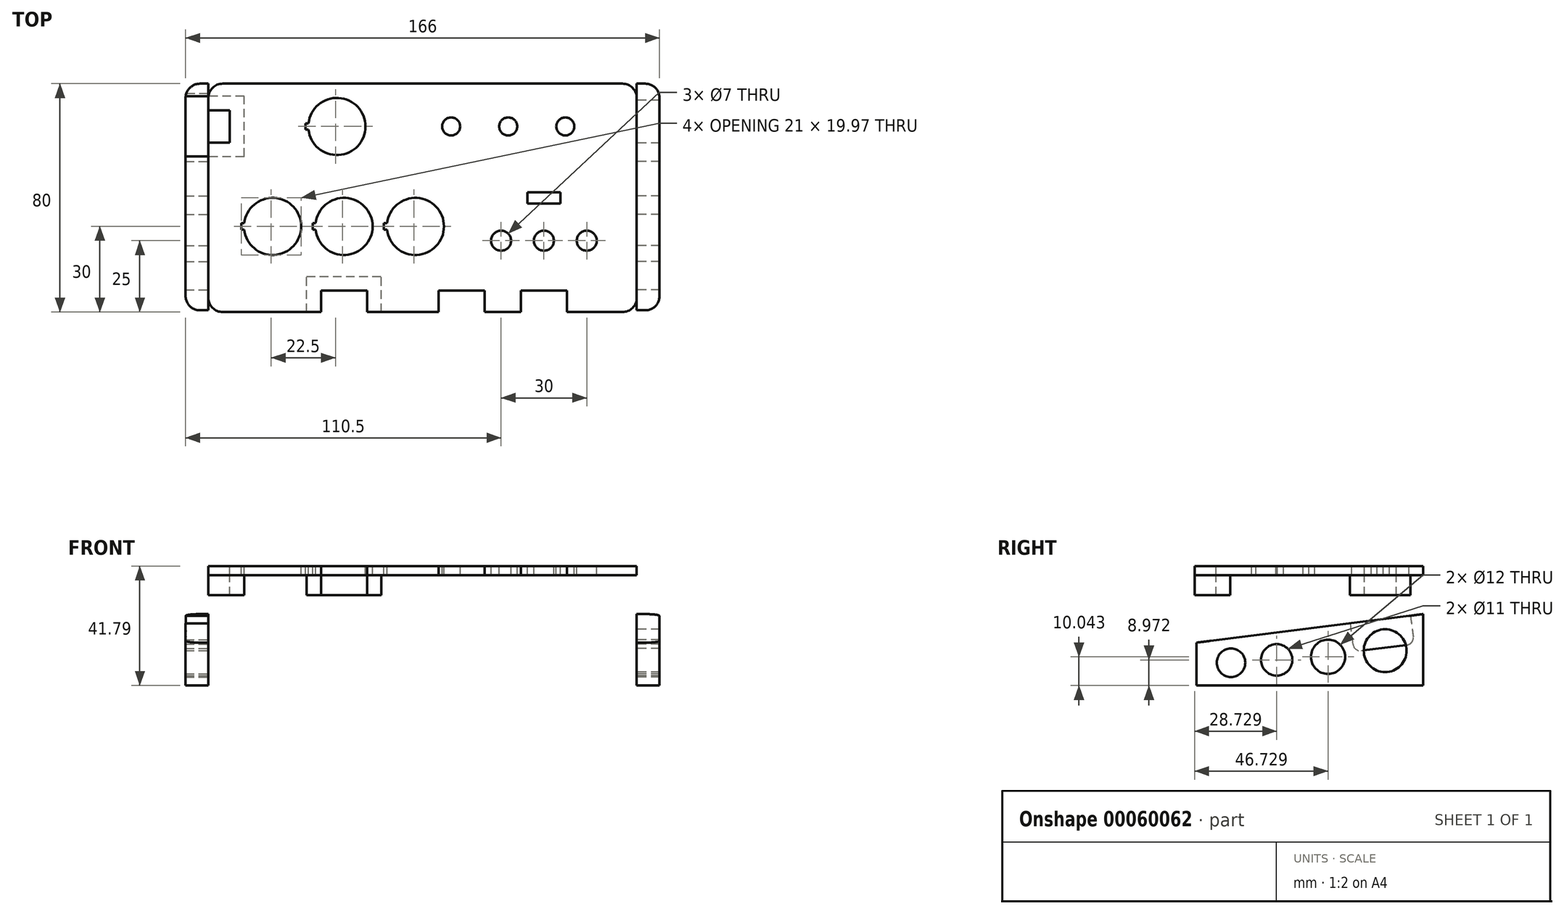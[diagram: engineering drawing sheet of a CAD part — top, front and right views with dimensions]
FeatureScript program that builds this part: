
annotation { "Feature Type Name" : "Feature", "Feature Type Description" : "" }
export const myFeature = defineFeature(function(context is Context, id is Id, definition is map)
    precondition{}
    {
        {
            var Q0;
            Q0=qCreatedBy(makeId("Top.planeOp"),FACE);
            var sketch = newSketch(context, id + "F0", { "sketchPlane" : qUnion([Q0])});
            skLineSegment(sketch, "E0.rect.bottom", {"start": v(75, 40) * mm, "end": v(-75, 40) * mm});
            skLineSegment(sketch, "E0.rect.top", {"start": v(75, -40) * mm, "end": v(-75, -40) * mm});
            skLineSegment(sketch, "E0.rect.left", {"start": v(75, 40) * mm, "end": v(75, -40) * mm});
            skLineSegment(sketch, "E0.rect.right", {"start": v(-75, 40) * mm, "end": v(-75, -40) * mm});
            skPoint(sketch, "E0.rect.middle", {"position": v(0, 0) * mm});
            skSolve(sketch);
        }
        {
            var Q0;
            Q0 = qSketchRegion(id + "F0", true);
            extrude(context, id + "F1", {"entities" : qUnion([Q0]), "depth" : 3.17 * mm});
        }
        {
            var Q0;
            Q0=makeQuery(id+"F1.opExtrude","SWEPT_EDGE",EDGE,{"disambiguationData":[OSD([sQuery(id+"F0.wireOp",EDGE,"E0.rect.bottom"),sQuery(id+"F0.wireOp",EDGE,"E0.rect.right")])]});
            var Q1;
            Q1=makeQuery(id+"F1.opExtrude","SWEPT_EDGE",EDGE,{"disambiguationData":[OSD([sQuery(id+"F0.wireOp",EDGE,"E0.rect.top"),sQuery(id+"F0.wireOp",EDGE,"E0.rect.right")])]});
            var Q2;
            Q2=makeQuery(id+"F1.opExtrude","SWEPT_EDGE",EDGE,{"disambiguationData":[OSD([sQuery(id+"F0.wireOp",EDGE,"E0.rect.top"),sQuery(id+"F0.wireOp",EDGE,"E0.rect.left")])]});
            var Q3;
            Q3=makeQuery(id+"F1.opExtrude","SWEPT_EDGE",EDGE,{"disambiguationData":[OSD([sQuery(id+"F0.wireOp",EDGE,"E0.rect.bottom"),sQuery(id+"F0.wireOp",EDGE,"E0.rect.left")])]});
            fillet(context, id + "F2", {"entities" : qUnion([Q0, Q1, Q2, Q3]), "radius" : 5 * mm, "tangentPropagation" : true, "allowEdgeOverflow" : false});
        }
        {
            var Q0;
            Q0=makeQuery(id+"F1.opExtrude","CAP_FACE",FACE,{"disambiguationData":[OSD([sQuery(id+"F0.wireOp",EDGE,"E0.rect.bottom"),sQuery(id+"F0.wireOp",EDGE,"E0.rect.top"),sQuery(id+"F0.wireOp",EDGE,"E0.rect.left"),sQuery(id+"F0.wireOp",EDGE,"E0.rect.right")])],"isStart":false});
            var sketch = newSketch(context, id + "F3", { "sketchPlane" : qUnion([Q0])});
            skArc(sketch, "E1", {"start": v(-39.94, 23.9) * mm, "mid": v(-20, 25) * mm, "end": v(-39.94, 26.1) * mm});
            skArc(sketch, "E2", {"start": v(-62.44, -11.1) * mm, "mid": v(-42.5, -10) * mm, "end": v(-62.44, -8.9) * mm});
            skArc(sketch, "E3", {"start": v(-37.44, -11.1) * mm, "mid": v(-17.5, -10) * mm, "end": v(-37.44, -8.9) * mm});
            skArc(sketch, "E4", {"start": v(-12.44, -11.1) * mm, "mid": v(7.5, -10) * mm, "end": v(-12.44, -8.9) * mm});
            skCircle(sketch, "E5", {"center": v(27.5, -15) * mm, "radius": 3.5 * mm});
            skCircle(sketch, "E6", {"center": v(42.5, -15) * mm, "radius": 3.5 * mm});
            skCircle(sketch, "E7", {"center": v(57.5, -15) * mm, "radius": 3.5 * mm});
            skCircle(sketch, "E8", {"center": v(10, 25) * mm, "radius": 3.18 * mm});
            skCircle(sketch, "E9", {"center": v(30, 25) * mm, "radius": 3.18 * mm});
            skCircle(sketch, "E10", {"center": v(50, 25) * mm, "radius": 3.18 * mm});
            skLineSegment(sketch, "E11", {"start": v(20, 17.63) * mm, "end": v(20, -10) * mm, "construction": true});
            skLineSegment(sketch, "E12.rect.bottom", {"start": v(48.3, 2) * mm, "end": v(36.7, 2) * mm});
            skLineSegment(sketch, "E12.rect.top", {"start": v(48.3, -2) * mm, "end": v(36.7, -2) * mm});
            skLineSegment(sketch, "E12.rect.left", {"start": v(48.3, 2) * mm, "end": v(48.3, -2) * mm});
            skLineSegment(sketch, "E12.rect.right", {"start": v(36.7, 2) * mm, "end": v(36.7, -2) * mm});
            skPoint(sketch, "E12.rect.middle", {"position": v(42.5, 0) * mm});
            skLineSegment(sketch, "E13.top", {"start": v(-63.5, -11.1) * mm, "end": v(-63.5, -8.9) * mm});
            skLineSegment(sketch, "E13.left", {"start": v(-62.44, -11.1) * mm, "end": v(-63.5, -11.1) * mm});
            skLineSegment(sketch, "E13.right", {"start": v(-62.44, -8.9) * mm, "end": v(-63.5, -8.9) * mm});
            skLineSegment(sketch, "E14.top", {"start": v(-38.5, -11.1) * mm, "end": v(-38.5, -8.9) * mm});
            skLineSegment(sketch, "E14.left", {"start": v(-37.44, -11.1) * mm, "end": v(-38.5, -11.1) * mm});
            skLineSegment(sketch, "E14.right", {"start": v(-37.44, -8.9) * mm, "end": v(-38.5, -8.9) * mm});
            skLineSegment(sketch, "E15.top", {"start": v(-13.5, -11.1) * mm, "end": v(-13.5, -8.9) * mm});
            skLineSegment(sketch, "E15.left", {"start": v(-12.44, -11.1) * mm, "end": v(-13.5, -11.1) * mm});
            skLineSegment(sketch, "E15.right", {"start": v(-12.44, -8.9) * mm, "end": v(-13.5, -8.9) * mm});
            skLineSegment(sketch, "E16.bottom", {"start": v(-39.94, 26.1) * mm, "end": v(-41, 26.1) * mm});
            skLineSegment(sketch, "E16.top", {"start": v(-39.94, 23.9) * mm, "end": v(-41, 23.9) * mm});
            skLineSegment(sketch, "E16.right", {"start": v(-41, 26.1) * mm, "end": v(-41, 23.9) * mm});
            skSolve(sketch);
        }
        {
            var Q0;
            Q0 = qSketchRegion(id + "F3", true);
            extrude(context, id + "F4", {"entities" : qUnion([Q0]), "operationType" : NewBodyOperationType.REMOVE, "endBound" : BoundingType.THROUGH_ALL, "oppositeDirection" : true, "depth" : 25 * mm});
        }
        {
            var Q0;
            Q0=makeQuery(id+"F1.opExtrude","CAP_FACE",FACE,{"disambiguationData":[OSD([sQuery(id+"F0.wireOp",EDGE,"E0.rect.bottom"),sQuery(id+"F0.wireOp",EDGE,"E0.rect.top"),sQuery(id+"F0.wireOp",EDGE,"E0.rect.left"),sQuery(id+"F0.wireOp",EDGE,"E0.rect.right")])],"isStart":false});
            var sketch = newSketch(context, id + "F5", { "sketchPlane" : qUnion([Q0])});
            skLineSegment(sketch, "E17.bottom", {"start": v(-75, 30.6) * mm, "end": v(-67.5, 30.6) * mm});
            skLineSegment(sketch, "E17.top", {"start": v(-75, 19.4) * mm, "end": v(-67.5, 19.4) * mm});
            skLineSegment(sketch, "E17.left", {"start": v(-75, 30.6) * mm, "end": v(-75, 19.4) * mm});
            skLineSegment(sketch, "E17.right", {"start": v(-67.5, 30.6) * mm, "end": v(-67.5, 19.4) * mm});
            skLineSegment(sketch, "E18", {"start": v(-67.5, 25) * mm, "end": v(-30, 25) * mm, "construction": true});
            skLineSegment(sketch, "E19.bottom", {"start": v(-35.6, -40) * mm, "end": v(-19.4, -40) * mm});
            skLineSegment(sketch, "E19.top", {"start": v(-35.6, -32.5) * mm, "end": v(-19.4, -32.5) * mm});
            skLineSegment(sketch, "E19.left", {"start": v(-35.6, -40) * mm, "end": v(-35.6, -32.5) * mm});
            skLineSegment(sketch, "E19.right", {"start": v(-19.4, -40) * mm, "end": v(-19.4, -32.5) * mm});
            skLineSegment(sketch, "E20.bottom", {"start": v(34.4, -40) * mm, "end": v(50.6, -40) * mm});
            skLineSegment(sketch, "E20.top", {"start": v(34.4, -32.5) * mm, "end": v(50.6, -32.5) * mm});
            skLineSegment(sketch, "E20.left", {"start": v(34.4, -40) * mm, "end": v(34.4, -32.5) * mm});
            skLineSegment(sketch, "E20.right", {"start": v(50.6, -40) * mm, "end": v(50.6, -32.5) * mm});
            skLineSegment(sketch, "E21.bottom", {"start": v(5.6, -40) * mm, "end": v(21.8, -40) * mm});
            skLineSegment(sketch, "E21.top", {"start": v(5.6, -32.5) * mm, "end": v(21.8, -32.5) * mm});
            skLineSegment(sketch, "E21.left", {"start": v(5.6, -40) * mm, "end": v(5.6, -32.5) * mm});
            skLineSegment(sketch, "E21.right", {"start": v(21.8, -40) * mm, "end": v(21.8, -32.5) * mm});
            skLineSegment(sketch, "E22", {"start": v(-27.5, -10) * mm, "end": v(-27.5, -32.5) * mm, "construction": true});
            skLineSegment(sketch, "E23", {"start": v(42.5, -15) * mm, "end": v(42.5, -32.5) * mm, "construction": true});
            skSolve(sketch);
        }
        {
            var Q0;
            Q0 = qSketchRegion(id + "F5", true);
            extrude(context, id + "F6", {"entities" : qUnion([Q0]), "operationType" : NewBodyOperationType.REMOVE, "endBound" : BoundingType.THROUGH_ALL, "oppositeDirection" : true, "depth" : 25 * mm});
        }
        {
            var Q0;
            Q0=qCreatedBy(makeId("Top.planeOp"),FACE);
            var sketch = newSketch(context, id + "F7", { "sketchPlane" : qUnion([Q0])});
            skLineSegment(sketch, "E24.rect.bottom", {"start": v(-62.5, 14.4) * mm, "end": v(-75, 14.4) * mm});
            skLineSegment(sketch, "E24.rect.top", {"start": v(-62.5, 35.6) * mm, "end": v(-75, 35.6) * mm});
            skLineSegment(sketch, "E24.rect.left", {"start": v(-62.5, 14.4) * mm, "end": v(-62.5, 35.6) * mm});
            skLineSegment(sketch, "E24.rect.right", {"start": v(-75, 14.4) * mm, "end": v(-75, 19.4) * mm});
            skLineSegment(sketch, "E25.bottom", {"start": v(-75, 30.6) * mm, "end": v(-67.5, 30.6) * mm});
            skLineSegment(sketch, "E25.top", {"start": v(-75, 19.4) * mm, "end": v(-67.5, 19.4) * mm});
            skLineSegment(sketch, "E25.right", {"start": v(-67.5, 30.6) * mm, "end": v(-67.5, 19.4) * mm});
            skLineSegment(sketch, "E26.trimOffspring", {"start": v(-75, 30.6) * mm, "end": v(-75, 35.6) * mm});
            skSolve(sketch);
        }
        {
            var Q0;
            Q0 = qSketchRegion(id + "F7", true);
            extrude(context, id + "F8", {"entities" : qUnion([Q0]), "oppositeDirection" : true, "depth" : 7 * mm});
        }
        {
            var Q0;
            Q0=qCreatedBy(makeId("Top.planeOp"),FACE);
            var sketch = newSketch(context, id + "F9", { "sketchPlane" : qUnion([Q0])});
            skLineSegment(sketch, "E27.top", {"start": v(-35.6, -32.5) * mm, "end": v(-19.4, -32.5) * mm});
            skLineSegment(sketch, "E27.left", {"start": v(-35.6, -40) * mm, "end": v(-35.6, -32.5) * mm});
            skLineSegment(sketch, "E27.right", {"start": v(-19.4, -40) * mm, "end": v(-19.4, -32.5) * mm});
            skLineSegment(sketch, "E28.bottom", {"start": v(-40.6, -40) * mm, "end": v(-35.6, -40) * mm});
            skLineSegment(sketch, "E28.top", {"start": v(-40.6, -27.5) * mm, "end": v(-14.4, -27.5) * mm});
            skLineSegment(sketch, "E28.left", {"start": v(-40.6, -40) * mm, "end": v(-40.6, -27.5) * mm});
            skLineSegment(sketch, "E28.right", {"start": v(-14.4, -40) * mm, "end": v(-14.4, -27.5) * mm});
            skLineSegment(sketch, "E29.trimOffspring", {"start": v(-19.4, -40) * mm, "end": v(-14.4, -40) * mm});
            skSolve(sketch);
        }
        {
            var Q0;
            Q0 = qSketchRegion(id + "F9", true);
            extrude(context, id + "F10", {"entities" : qUnion([Q0]), "oppositeDirection" : true, "depth" : 7 * mm});
        }
        {
            var Q0;
            Q0=makeQuery(id+"F1.opExtrude","SWEPT_FACE",FACE,{"disambiguationData":[OSD([sQuery(id+"F0.wireOp",EDGE,"E0.rect.left")])]});
            var sketch = newSketch(context, id + "F11", { "sketchPlane" : qUnion([Q0])});
            skLineSegment(sketch, "E30.bottom", {"start": v(40, -13.61) * mm, "end": v(-39.37, -23.61) * mm});
            skLineSegment(sketch, "E30.top", {"start": v(40, -38.61) * mm, "end": v(-39.37, -38.61) * mm});
            skLineSegment(sketch, "E30.left", {"start": v(40, -13.61) * mm, "end": v(40, -38.61) * mm});
            skLineSegment(sketch, "E30.right", {"start": v(-39.37, -23.61) * mm, "end": v(-39.37, -38.61) * mm});
            skCircle(sketch, "E31", {"center": v(26.73, -26.43) * mm, "radius": 7.5 * mm});
            skCircle(sketch, "E32", {"center": v(6.73, -28.57) * mm, "radius": 6 * mm});
            skCircle(sketch, "E33", {"center": v(-27.27, -30.65) * mm, "radius": 5 * mm});
            skLineSegment(sketch, "E34", {"start": v(-27.06, -35.64) * mm, "end": v(26.97, -33.93) * mm, "construction": true});
            skCircle(sketch, "E35", {"center": v(-11.27, -29.64) * mm, "radius": 5.5 * mm});
            skSolve(sketch);
        }
        {
            var Q0;
            Q0=makeQuery(id+"F11.imprint","IMPRINT",FACE,{"disambiguationData":[TD([[makeQuery(id+"F11.imprint","IMPRINT",EDGE,{"derivedFrom":sQuery(id+"F11.wireOp",EDGE,"E30.bottom")}),1.0]])]});
            extrude(context, id + "F12", {"entities" : qUnion([Q0]), "depth" : 8 * mm});
        }
        {
            var Q0;
            {var subQ0=sQuery(id+"F0.wireOp",EDGE,"E0.rect.right");Q0=makeQuery(id+"F6.boolean.opBoolean","SPLIT",FACE,{"disambiguationData":[TD([makeQuery(id+"F6.opExtrude","SWEPT_FACE",FACE,{"disambiguationData":[OSD([sQuery(id+"F5.wireOp",EDGE,"E17.top")])]})])],"derivedFrom":makeQuery(id+"F1.opExtrude","SWEPT_FACE",FACE,{"disambiguationData":[OSD([subQ0])]})});}
            var sketch = newSketch(context, id + "F13", { "sketchPlane" : qUnion([Q0])});
            skLineSegment(sketch, "E36", {"start": v(-40, -13.61) * mm, "end": v(-40, -38.61) * mm});
            skLineSegment(sketch, "E37", {"start": v(39.37, -38.61) * mm, "end": v(-40, -38.61) * mm});
            skLineSegment(sketch, "E38", {"start": v(39.37, -38.61) * mm, "end": v(39.37, -23.61) * mm});
            skLineSegment(sketch, "E39", {"start": v(-14.57, -16.81) * mm, "end": v(39.37, -23.61) * mm});
            skLineSegment(sketch, "E40", {"start": v(-35.6, -14.16) * mm, "end": v(-36.85, -24.09) * mm});
            skLineSegment(sketch, "E41", {"start": v(-15.82, -26.74) * mm, "end": v(-36.85, -24.09) * mm});
            skLineSegment(sketch, "E42", {"start": v(-15.82, -26.74) * mm, "end": v(-14.57, -16.81) * mm});
            skLineSegment(sketch, "E43.trimOffspring", {"start": v(-40, -13.61) * mm, "end": v(-35.6, -14.16) * mm});
            skCircle(sketch, "E44", {"center": v(-6.73, -28.57) * mm, "radius": 6 * mm});
            skCircle(sketch, "E45", {"center": v(11.27, -29.64) * mm, "radius": 5.5 * mm});
            skCircle(sketch, "E46", {"center": v(27.27, -30.65) * mm, "radius": 5 * mm});
            skSolve(sketch);
        }
        {
            var Q0;
            Q0 = qSketchRegion(id + "F13", true);
            extrude(context, id + "F14", {"entities" : qUnion([Q0]), "depth" : 8 * mm});
        }
        {
            var Q0;
            Q0=makeQuery(id+"F12.opExtrude","CAP_EDGE",EDGE,{"disambiguationData":[OSD([sQuery(id+"F11.wireOp",EDGE,"E30.right")])],"isStart":false});
            var Q1;
            Q1=makeQuery(id+"F12.opExtrude","CAP_EDGE",EDGE,{"disambiguationData":[OSD([sQuery(id+"F11.wireOp",EDGE,"E30.left")])],"isStart":false});
            var Q2;
            Q2=makeQuery(id+"F14.opExtrude","CAP_EDGE",EDGE,{"disambiguationData":[OSD([sQuery(id+"F13.wireOp",EDGE,"E36")])],"isStart":false});
            var Q3;
            Q3=makeQuery(id+"F14.opExtrude","CAP_EDGE",EDGE,{"disambiguationData":[OSD([sQuery(id+"F13.wireOp",EDGE,"E38")])],"isStart":false});
            fillet(context, id + "F15", {"entities" : qUnion([Q0, Q1, Q2, Q3]), "radius" : 5 * mm, "tangentPropagation" : true, "allowEdgeOverflow" : false});
        }
        {
            var Q0;
            Q0=makeQuery(id+"F14.opExtrude","SWEPT_EDGE",EDGE,{"disambiguationData":[OSD([sQuery(id+"F13.wireOp",EDGE,"E41"),sQuery(id+"F13.wireOp",EDGE,"E42")])]});
            var Q1;
            Q1=makeQuery(id+"F14.opExtrude","SWEPT_EDGE",EDGE,{"disambiguationData":[OSD([sQuery(id+"F13.wireOp",EDGE,"E40"),sQuery(id+"F13.wireOp",EDGE,"E41")])]});
            fillet(context, id + "F16", {"entities" : qUnion([Q0, Q1]), "radius" : 2.5 * mm, "tangentPropagation" : true, "allowEdgeOverflow" : false});
        }
    });
